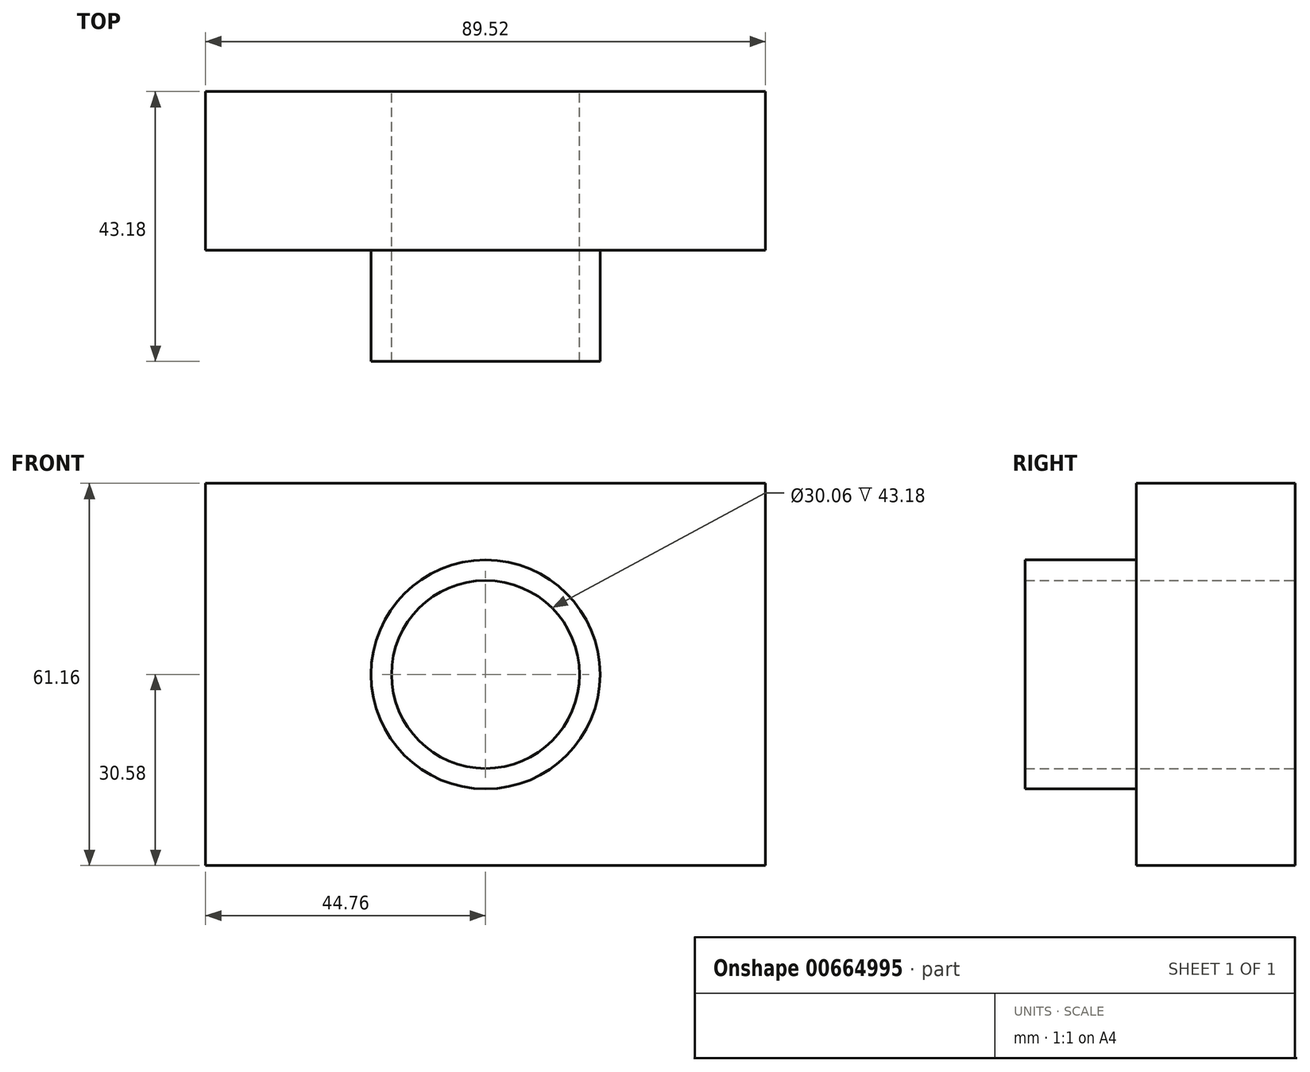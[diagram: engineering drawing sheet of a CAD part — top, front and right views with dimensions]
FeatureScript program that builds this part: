
annotation { "Feature Type Name" : "Feature", "Feature Type Description" : "" }
export const myFeature = defineFeature(function(context is Context, id is Id, definition is map)
    precondition{}
    {
        {
            var Q0;
            Q0=qCreatedBy(makeId("Front.planeOp"),FACE);
            var sketch = newSketch(context, id + "F0", { "sketchPlane" : qUnion([Q0])});
            skLineSegment(sketch, "E0.bottom", {"start": v(-44.76, 30.58) * mm, "end": v(44.76, 30.58) * mm});
            skLineSegment(sketch, "E0.top", {"start": v(-44.76, -30.58) * mm, "end": v(44.76, -30.58) * mm});
            skLineSegment(sketch, "E0.left", {"start": v(-44.76, 30.58) * mm, "end": v(-44.76, -30.58) * mm});
            skLineSegment(sketch, "E0.right", {"start": v(44.76, 30.58) * mm, "end": v(44.76, -30.58) * mm});
            skPoint(sketch, "E0.middle", {"position": v(0, 0) * mm});
            skCircle(sketch, "E1", {"center": v(0, 0) * mm, "radius": 18.31 * mm});
            skCircle(sketch, "E2", {"center": v(0, 0) * mm, "radius": 15.03 * mm});
            skSolve(sketch);
        }
        {
            var Q0;
            Q0=makeQuery(id+"F0.imprint","IMPRINT",FACE,{"disambiguationData":[TD([[makeQuery(id+"F0.imprint","IMPRINT",EDGE,{"derivedFrom":sQuery(id+"F0.wireOp",EDGE,"E0.bottom")}),-1.0]])]});
            var Q1;
            Q1=makeQuery(id+"F0.imprint","IMPRINT",FACE,{"disambiguationData":[TD([[makeQuery(id+"F0.imprint","IMPRINT",EDGE,{"derivedFrom":sQuery(id+"F0.wireOp",EDGE,"E1")}),1.0]])]});
            extrude(context, id + "F1", {"entities" : qUnion([Q0, Q1]), "depth" : 25.4 * mm, "offsetDistance" : 25.4 * mm});
        }
        {
            var Q0;
            Q0=makeQuery(id+"F0.imprint","IMPRINT",FACE,{"disambiguationData":[TD([[makeQuery(id+"F0.imprint","IMPRINT",EDGE,{"derivedFrom":sQuery(id+"F0.wireOp",EDGE,"E1")}),1.0]])]});
            extrude(context, id + "F2", {"entities" : qUnion([Q0]), "operationType" : NewBodyOperationType.ADD, "depth" : 43.18 * mm, "offsetDistance" : 25.4 * mm});
        }
    });
